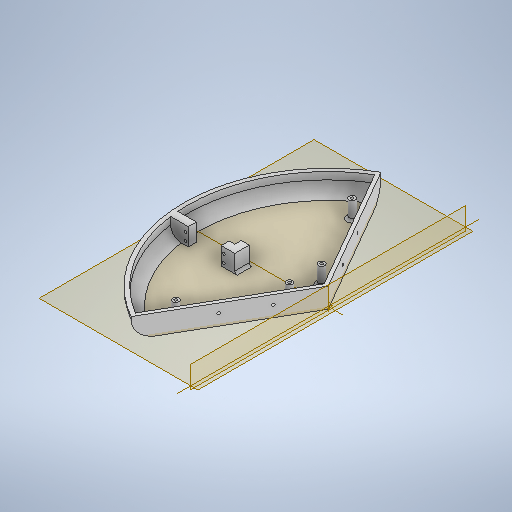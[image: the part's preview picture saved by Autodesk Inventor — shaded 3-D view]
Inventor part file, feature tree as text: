
AUTODESK INVENTOR PART (.ipt)
format: ipt  version: 2025.1 (Build 291241000, 241)  size: 467,968 bytes
history: native  units: mm
features: extrude x10, sketch x10, fillet x4
ambient origin geometry x8: Origin, YZ Plane, XZ Plane, XY Plane, X Axis, Y Axis, Z Axis, Center Point
bodies: Solid1 (feature_tree)
feature tree (24):
  extrude  "Extrusion1"  TaperAngle=60.0deg  [1 undecoded]
  extrude  "Extrusion2"  Depth=22.0mm TaperAngle=0.0deg
  extrude  "Extrusion4"  TaperAngle=0.0deg  [1 undecoded]
  extrude  "Extrusion5"  Depth=3.3mm
  extrude  "Extrusion8"  Depth=15.0mm TaperAngle=0.0deg
  extrude  "Extrusion9"  Depth=3.3mm
  extrude  "Extrusion10"  Depth=3.0mm TaperAngle=0.0deg
  fillet  "Rundung2"  Radius=3.0mm
  fillet  "Rundung3"  Radius=13.0mm
  extrude  "Extrusion11"  Depth=41.0mm
  extrude  "Extrusion12"  TaperAngle=120.0deg  [1 undecoded]
  fillet  "Rundung4"  Radius=41.0mm
  fillet  "Rundung5"  Radius=3.0mm
  extrude  "Extrusion13"  [1 undecoded]
  sketch  "Sketch1"  dims[d3=180.0mm d4=60.0deg]
  sketch  "Sketch4"  dims[d5=120.0deg d7=22.0mm d8=0.0mm]
  sketch  "Sketch8"  dims[d43=160.0mm d47=0.0mm d48=0.0mm]
  sketch  "Sketch9"  dims[d68=3.3mm d69=3.3mm]
  sketch  "Sketch12"  dims[d70=50.0mm d72=15.0mm d73=0.0mm]
  sketch  "Skizze13"  dims[d74=3.3mm d75=3.3mm]
  sketch  "Skizze15"  dims[d76=50.0mm d78=15.0mm d79=0.0mm d93=3.0mm d94=0.0mm d98=13.0mm]
  sketch  "Skizze16"  dims[d99=55.0mm d101=41.0mm]
  sketch  "Skizze17"  dims[d102=110.5mm d103=120.0deg d104=41.0mm d105=3.0mm]
  sketch  "Skizze19"  dims[d106=5.0mm d109=-2.0mm d110=0.0mm d111=10.0mm d112=22.0mm d113=0.0mm d115=350.0mm d116=120.0deg d117=10.0mm d118=10.0mm d119=10.0mm d120=22.0mm d121=0.0mm d122=13.0mm d123=22.0mm d127=10.0mm d128=8.0mm d129=8.0mm d130=10.0mm d131=90.0mm d132=20.0mm d133=8.0mm d134=8.0mm d135=90.0mm d136=20.0mm d137=10.0mm d138=10.0mm d139=22.0mm d140=0.0mm d141=3.6mm d142=5.0mm d143=0.0mm d144=3.0mm d145=3.0mm d146=10.0mm d147=10.0mm d148=3.3mm d149=3.3mm d150=3.3mm d151=3.3mm d153=3.4mm d154=3.4mm d155=3.4mm d156=3.4mm d157=4.8mm d158=4.8mm d159=5.0mm d160=0.0mm d161=50.0mm d162=50.0mm d54=1.0mm d55=1.0mm d56=1.0mm d57=0.15mm d58=0.25mm d59=0.375mm d60=14.3117mm d61=0.75mm d62=20.594885mm d63=0.0625mm d64=0.75mm d65=0.375mm d85=0.5mm d86=0.872665mm d87=0.5mm d88=0.872665mm d96=0.5mm d97=0.872665mm]
note: 4 required parameter values undecoded (feature->parameter linkage not recoverable at this tier; creation-order binding heuristic only, values carry confidence <= 0.55)
